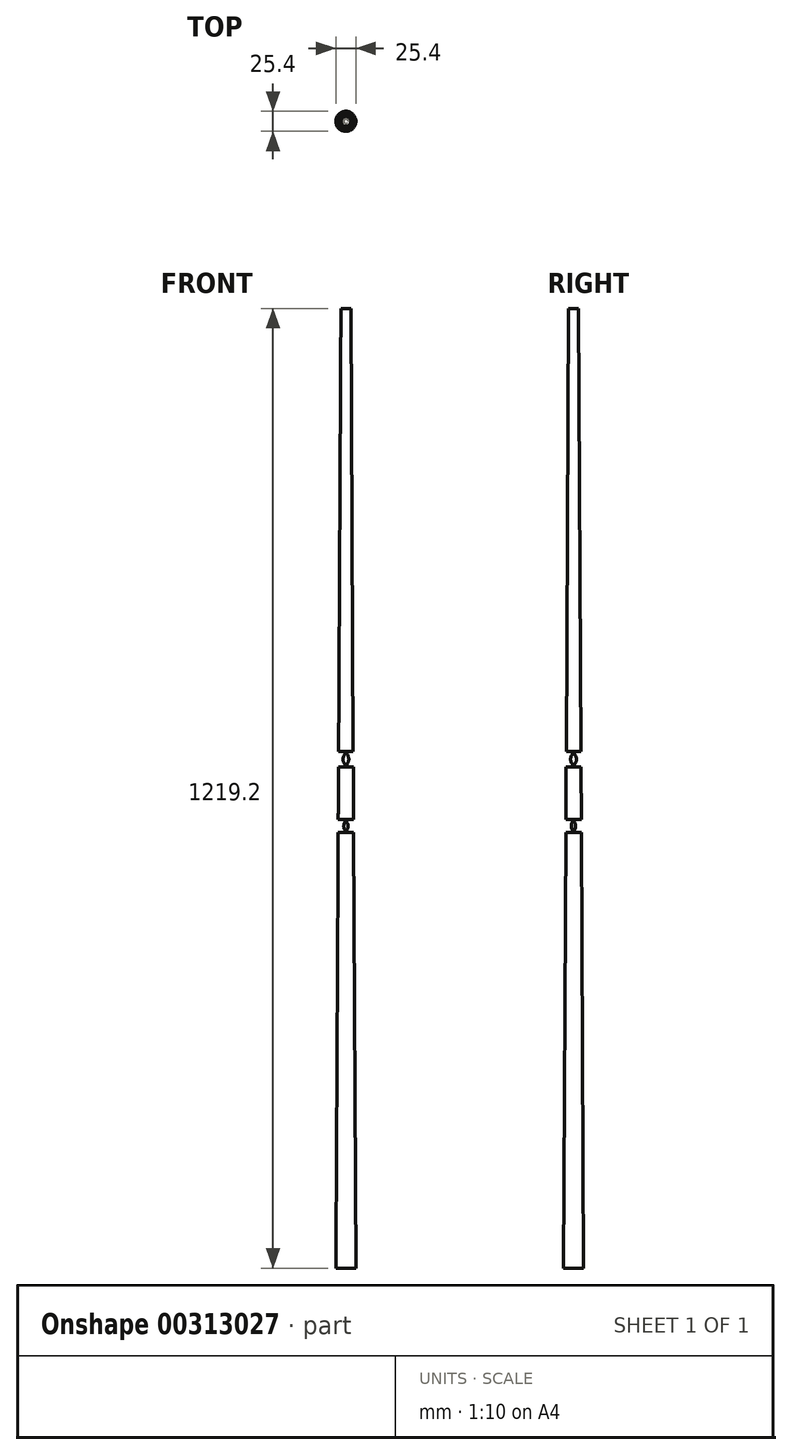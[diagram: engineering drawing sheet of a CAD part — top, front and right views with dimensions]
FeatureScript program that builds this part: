
annotation { "Feature Type Name" : "Feature", "Feature Type Description" : "" }
export const myFeature = defineFeature(function(context is Context, id is Id, definition is map)
    precondition{}
    {
        {
            var Q0;
            Q0=qCreatedBy(makeId("Front.planeOp"),FACE);
            var sketch = newSketch(context, id + "F0", { "sketchPlane" : qUnion([Q0])});
            skLineSegment(sketch, "E0", {"start": v(-15.3, -68.82) * mm, "end": v(-2.6, -68.82) * mm});
            skLineSegment(sketch, "E1", {"start": v(-2.6, -68.82) * mm, "end": v(-2.6, 1150.38) * mm});
            skLineSegment(sketch, "E2", {"start": v(-15.3, -68.82) * mm, "end": v(-8.95, 1150.38) * mm});
            skPoint(sketch, "E2.endSnap0", {"position": v(-8.95, -68.82) * mm});
            skLineSegment(sketch, "E3", {"start": v(-8.95, 1150.38) * mm, "end": v(-2.6, 1150.38) * mm});
            skArc(sketch, "E4", {"start": v(-12.33, 501.11) * mm, "mid": v(-17.87, 492.85) * mm, "end": v(-12.42, 484.54) * mm});
            skArc(sketch, "E5", {"start": v(-11.88, 587.34) * mm, "mid": v(-18.97, 577.8) * mm, "end": v(-11.98, 568.2) * mm});
            skSolve(sketch);
        }
        {
            var Q0;
            Q0 = qSketchRegion(id + "F0", true);
            var Q1;
            Q1=sQuery(id+"F0.wireOp",EDGE,"E1");
            revolve(context, id + "F1", {"entities" : qUnion([Q0]), "axis" : qUnion([Q1]), "revolveType" : RevolveType.FULL});
        }
    });
